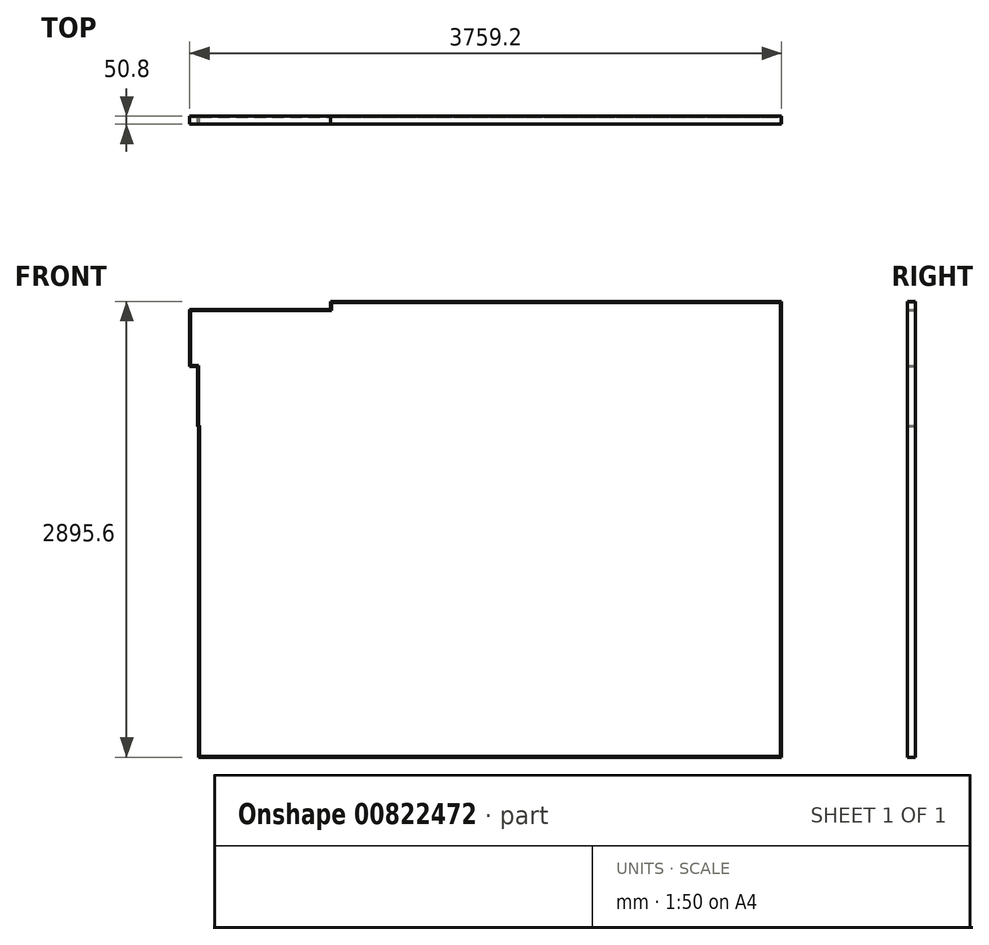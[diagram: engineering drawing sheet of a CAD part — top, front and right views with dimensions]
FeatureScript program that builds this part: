
annotation { "Feature Type Name" : "Feature", "Feature Type Description" : "" }
export const myFeature = defineFeature(function(context is Context, id is Id, definition is map)
    precondition{}
    {
        {
            var Q0;
            Q0=qCreatedBy(makeId("Front.planeOp"),FACE);
            var sketch = newSketch(context, id + "F0", { "sketchPlane" : qUnion([Q0])});
            skLineSegment(sketch, "E0.bottom", {"start": v(-918.62, 1009.3) * mm, "end": v(1945.23, 1009.3) * mm});
            skLineSegment(sketch, "E0.top", {"start": v(-1756.82, -1886.3) * mm, "end": v(1945.23, -1886.3) * mm});
            skLineSegment(sketch, "E0.right", {"start": v(1945.23, 1009.3) * mm, "end": v(1945.23, -1886.3) * mm});
            skLineSegment(sketch, "E1", {"start": v(-1813.97, 958.5) * mm, "end": v(-1813.97, 596.55) * mm});
            skLineSegment(sketch, "E2", {"start": v(-1813.97, 596.55) * mm, "end": v(-1763.17, 596.55) * mm});
            skLineSegment(sketch, "E3", {"start": v(-1763.17, 596.55) * mm, "end": v(-1763.17, 215.55) * mm});
            skLineSegment(sketch, "E4", {"start": v(-1763.17, 215.55) * mm, "end": v(-1756.82, 215.55) * mm});
            skLineSegment(sketch, "E5", {"start": v(-1756.82, 215.55) * mm, "end": v(-1756.82, -1886.3) * mm});
            skPoint(sketch, "E6.orphan", {"position": v(-1763.17, 0) * mm});
            skLineSegment(sketch, "E7", {"start": v(-918.62, 1009.3) * mm, "end": v(-918.62, 958.5) * mm});
            skLineSegment(sketch, "E8", {"start": v(-918.62, 958.5) * mm, "end": v(-1813.97, 958.5) * mm});
            skSolve(sketch);
        }
        {
            var Q0;
            Q0 = qSketchRegion(id + "F0", true);
            extrude(context, id + "F1", {"entities" : qUnion([Q0]), "depth" : 50.8 * mm, "offsetDistance" : 25.4 * mm});
        }
        {
            var Q0;
            Q0=makeQuery(id+"F1.opExtrude","CAP_FACE",FACE,{"disambiguationData":[OSD([sQuery(id+"F0.wireOp",EDGE,"E0.bottom"),sQuery(id+"F0.wireOp",EDGE,"E0.top"),sQuery(id+"F0.wireOp",EDGE,"E0.right"),sQuery(id+"F0.wireOp",EDGE,"E1"),sQuery(id+"F0.wireOp",EDGE,"E2"),sQuery(id+"F0.wireOp",EDGE,"E3"),sQuery(id+"F0.wireOp",EDGE,"E4"),sQuery(id+"F0.wireOp",EDGE,"E5"),sQuery(id+"F0.wireOp",EDGE,"E7"),sQuery(id+"F0.wireOp",EDGE,"E8")])],"isStart":false});
            shell(context, id + "F2", {"entities" : qUnion([Q0]), "thickness" : 6.35 * mm});
        }
    });
